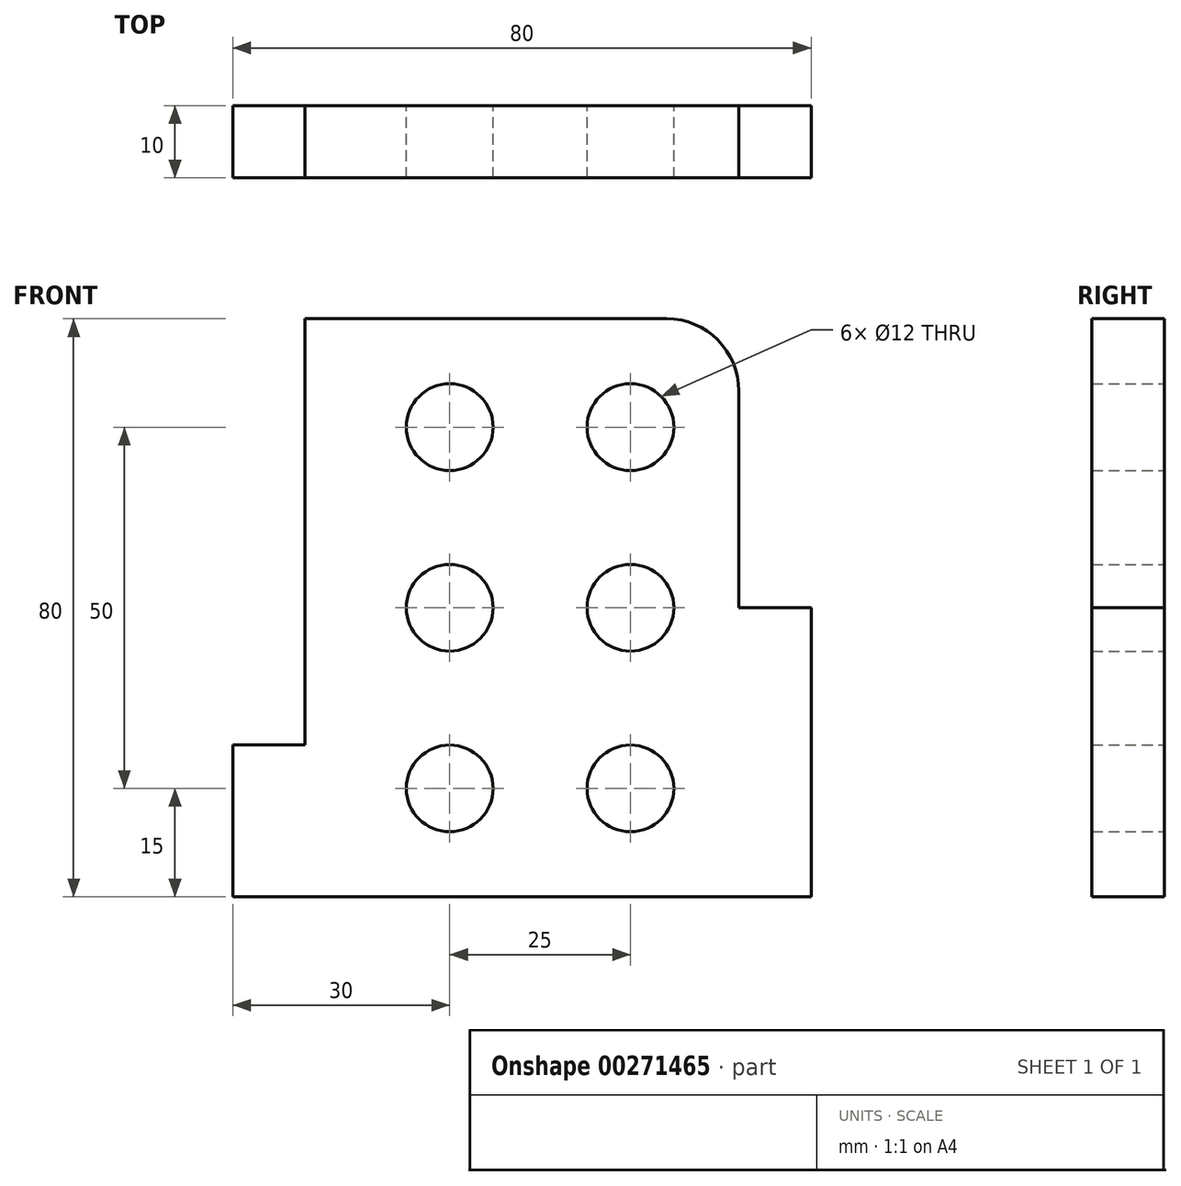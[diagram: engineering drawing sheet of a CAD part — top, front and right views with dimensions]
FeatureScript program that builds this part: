
annotation { "Feature Type Name" : "Feature", "Feature Type Description" : "" }
export const myFeature = defineFeature(function(context is Context, id is Id, definition is map)
    precondition{}
    {
        {
            var Q0;
            Q0=qCreatedBy(makeId("Front.planeOp"),FACE);
            var sketch = newSketch(context, id + "F0", { "sketchPlane" : qUnion([Q0])});
            skLineSegment(sketch, "E0", {"start": v(0, 0) * mm, "end": v(0, 21) * mm});
            skLineSegment(sketch, "E1", {"start": v(0, 21) * mm, "end": v(10, 21) * mm});
            skLineSegment(sketch, "E2", {"start": v(10, 21) * mm, "end": v(10, 80) * mm});
            skLineSegment(sketch, "E3", {"start": v(10, 80) * mm, "end": v(60, 80) * mm});
            skLineSegment(sketch, "E4", {"start": v(0, 0) * mm, "end": v(80, 0) * mm});
            skLineSegment(sketch, "E5", {"start": v(80, 0) * mm, "end": v(80, 40) * mm});
            skLineSegment(sketch, "E6", {"start": v(80, 40) * mm, "end": v(70, 40) * mm});
            skLineSegment(sketch, "E7", {"start": v(70, 40) * mm, "end": v(70, 70) * mm});
            skCircle(sketch, "E8", {"center": v(30, 15) * mm, "radius": 6 * mm});
            skCircle(sketch, "E9", {"center": v(30, 40) * mm, "radius": 6 * mm});
            skCircle(sketch, "E10", {"center": v(30, 65) * mm, "radius": 6 * mm});
            skCircle(sketch, "E11", {"center": v(55, 15) * mm, "radius": 6 * mm});
            skCircle(sketch, "E12", {"center": v(55, 40) * mm, "radius": 6 * mm});
            skCircle(sketch, "E13", {"center": v(55, 65) * mm, "radius": 6 * mm});
            skArc(sketch, "E14", {"start": v(60, 80) * mm, "mid": v(67.07, 77.07) * mm, "end": v(70, 70) * mm});
            skSolve(sketch);
        }
        {
            var Q0;
            Q0=makeQuery(id+"F0.imprint","IMPRINT",FACE,{"disambiguationData":[TD([[makeQuery(id+"F0.imprint","IMPRINT",EDGE,{"derivedFrom":sQuery(id+"F0.wireOp",EDGE,"E0")}),-1.0]])]});
            extrude(context, id + "F1", {"entities" : qUnion([Q0]), "depth" : 10 * mm});
        }
    });
